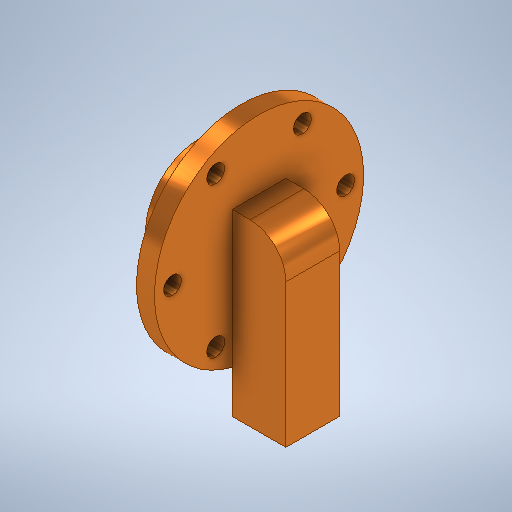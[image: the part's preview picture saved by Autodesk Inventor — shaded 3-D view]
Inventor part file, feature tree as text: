
AUTODESK INVENTOR PART (.ipt)
format: ipt  version: 2025.1 (Build 291241000, 241)  size: 334,336 bytes
history: native  units: mm
features: sketch x6, hole x4, revolve x1, extrude x1, plane x1, pattern_circular x1, projected_geometry x1
ambient origin geometry x8: Origin, YZ Plane, XZ Plane, XY Plane, X Axis, Y Axis, Z Axis, Center Point
bodies: Solid1 (feature_tree)
feature tree (15):
  revolve  "Revolution1"  [1 undecoded]
  extrude  "Extrusion1"  Depth=3.0mm
  hole  "Hole1"  [1 undecoded]
  plane  "Work Plane1"
  hole  "Hole2"  [1 undecoded]
  hole  "Hole3"  [1 undecoded]
  pattern_circular  "Circular Pattern1"  [2 undecoded]
  hole  "Hole4"  [1 undecoded]
  sketch  "Sketch1"  dims[d0=18.0mm d1=35.0mm]
  sketch  "Sketch2"  dims[d2=7.0mm d3=3.0mm]
  sketch  "Sketch3"  dims[d4=90.0deg d6=30.0mm]
  sketch  "Sketch4"  dims[d7=9.0mm d8=6.5mm]
  sketch  "Sketch5"  dims[d9=6.0mm d10=9.0mm d11=0.0mm]
  projected_geometry  "Projected Loop1"
  sketch  "Sketch6"  dims[d12=4.917mm d13=11.0mm d14=6.0mm d15=7.0mm d16=90.0deg d17=11.0mm d18=0.0mm d19=4.5mm d20=4.5mm d21=-7.5mm d22=1.5mm d23=11.0mm d24=4.0mm d25=2.0mm d26=90.0deg d27=7.5mm d28=0.0mm d29=29.0mm d30=30.0deg d31=3.0mm d32=6.0mm d33=4.0mm d34=2.0mm d35=90.0deg d36=7.5mm d37=0.0mm d38=60.0mm d39=360.0deg d41=1.5mm d42=6.0mm d43=4.0mm d44=2.0mm d45=90.0deg d46=14.5mm d47=0.0mm]
note: 7 required parameter values undecoded (feature->parameter linkage not recoverable at this tier; creation-order binding heuristic only, values carry confidence <= 0.55)